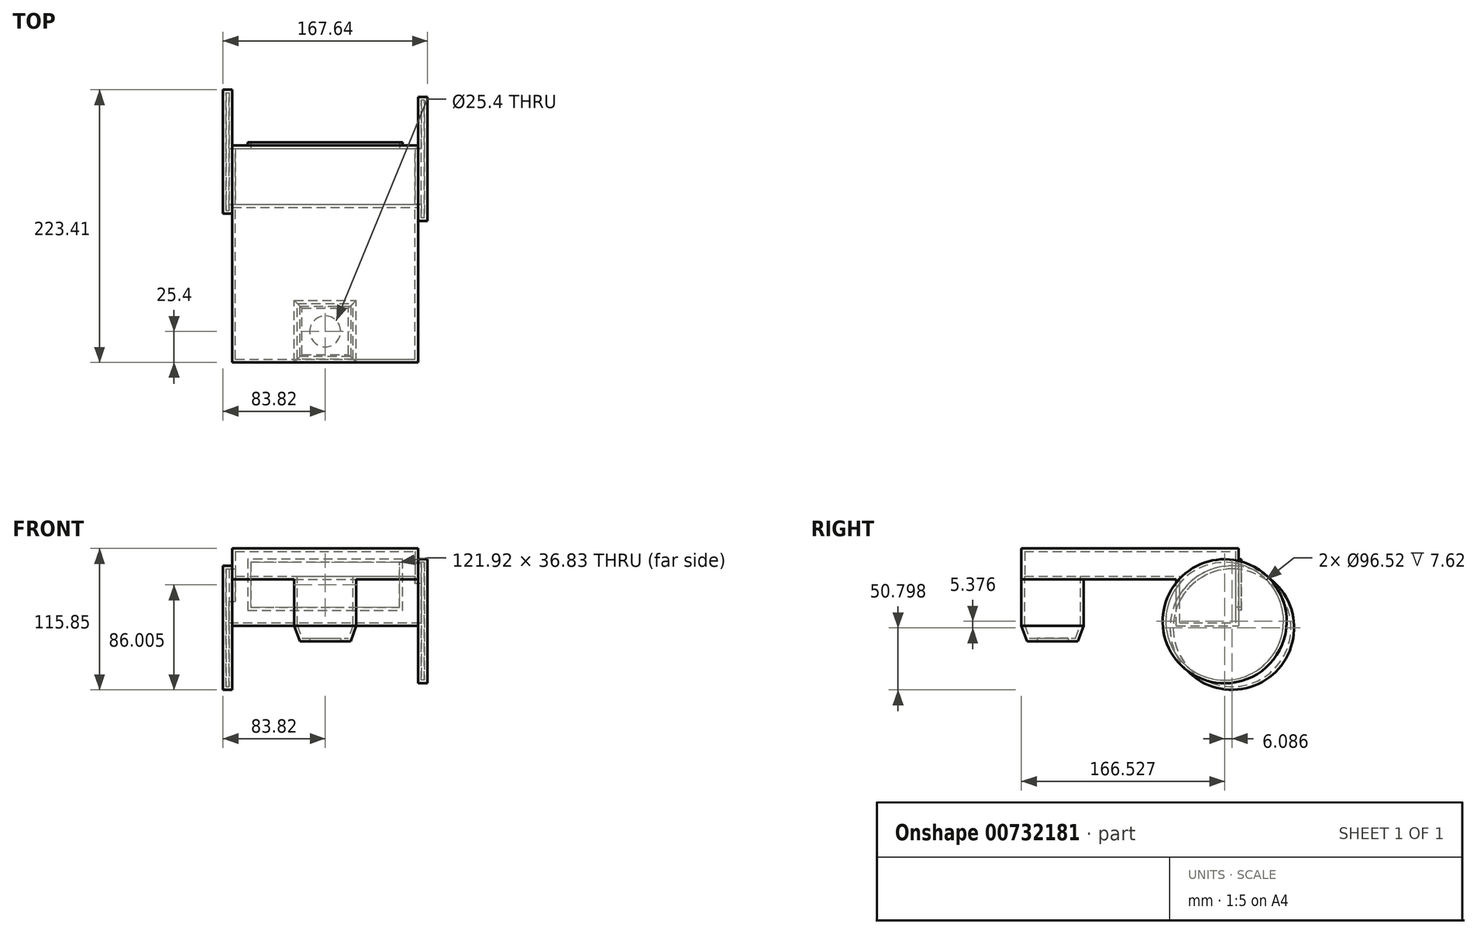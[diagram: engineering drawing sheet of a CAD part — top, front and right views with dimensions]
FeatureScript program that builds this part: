
annotation { "Feature Type Name" : "Feature", "Feature Type Description" : "" }
export const myFeature = defineFeature(function(context is Context, id is Id, definition is map)
    precondition{}
    {
        {
            var Q0;
            Q0=qCreatedBy(makeId("Front.planeOp"),FACE);
            var sketch = newSketch(context, id + "F0", { "sketchPlane" : qUnion([Q0])});
            skLineSegment(sketch, "E0.bottom", {"start": v(-101.6, 25.4) * mm, "end": v(50.8, 25.4) * mm});
            skLineSegment(sketch, "E0.top", {"start": v(-101.6, 0) * mm, "end": v(50.8, 0) * mm});
            skLineSegment(sketch, "E0.left", {"start": v(-101.6, 25.4) * mm, "end": v(-101.6, 0) * mm});
            skLineSegment(sketch, "E0.right", {"start": v(50.8, 25.4) * mm, "end": v(50.8, 0) * mm});
            skSolve(sketch);
        }
        {
            var Q0;
            Q0 = qSketchRegion(id + "F0", true);
            extrude(context, id + "F1", {"entities" : qUnion([Q0]), "depth" : 177.8 * mm, "offsetDistance" : 25.4 * mm});
        }
        {
            var Q0;
            Q0=makeQuery(id+"F1.opExtrude","SWEPT_FACE",FACE,{"disambiguationData":[OSD([sQuery(id+"F0.wireOp",EDGE,"E0.top")])]});
            var sketch = newSketch(context, id + "F2", { "sketchPlane" : qUnion([Q0])});
            skLineSegment(sketch, "E1.bottom", {"start": v(-50.8, 177.8) * mm, "end": v(0, 177.8) * mm});
            skLineSegment(sketch, "E1.top", {"start": v(-50.8, 127) * mm, "end": v(0, 127) * mm});
            skLineSegment(sketch, "E1.left", {"start": v(-50.8, 177.8) * mm, "end": v(-50.8, 127) * mm});
            skLineSegment(sketch, "E1.right", {"start": v(0, 177.8) * mm, "end": v(0, 127) * mm});
            skSolve(sketch);
        }
        {
            var Q0;
            Q0=makeQuery(id+"F2.imprint","IMPRINT",FACE,{"disambiguationData":[TD([[makeQuery(id+"F2.imprint","IMPRINT",EDGE,{"derivedFrom":sQuery(id+"F2.wireOp",EDGE,"E1.bottom")}),-1.0]])]});
            extrude(context, id + "F3", {"entities" : qUnion([Q0]), "operationType" : NewBodyOperationType.ADD, "depth" : 50.8 * mm, "offsetDistance" : 25.4 * mm});
        }
        {
            var Q0;
            Q0=makeQuery(id+"F3.opExtrude","CAP_EDGE",EDGE,{"disambiguationData":[OSD([sQuery(id+"F2.wireOp",EDGE,"E1.bottom")])],"isStart":false});
            var Q1;
            Q1=makeQuery(id+"F3.opExtrude","CAP_EDGE",EDGE,{"disambiguationData":[OSD([sQuery(id+"F2.wireOp",EDGE,"E1.left")])],"isStart":false});
            var Q2;
            Q2=makeQuery(id+"F3.opExtrude","CAP_EDGE",EDGE,{"disambiguationData":[OSD([sQuery(id+"F2.wireOp",EDGE,"E1.right")])],"isStart":false});
            var Q3;
            Q3=makeQuery(id+"F3.opExtrude","CAP_EDGE",EDGE,{"disambiguationData":[OSD([sQuery(id+"F2.wireOp",EDGE,"E1.top")])],"isStart":false});
            chamfer(context, id + "F4", {"entities" : qUnion([Q0, Q1, Q2, Q3]), "chamferType" : ChamferType.OFFSET_ANGLE, "width" : 12.7 * mm, "oppositeDirection" : false, "angle" : 20 * degree, "tangentPropagation" : true});
        }
        {
            var Q0;
            Q0=makeQuery(id+"F1.opExtrude","SWEPT_FACE",FACE,{"disambiguationData":[OSD([sQuery(id+"F0.wireOp",EDGE,"E0.top")])]});
            var sketch = newSketch(context, id + "F5", { "sketchPlane" : qUnion([Q0])});
            skLineSegment(sketch, "E2.bottom", {"start": v(-101.6, 0) * mm, "end": v(-63.5, 0) * mm});
            skLineSegment(sketch, "E2.top", {"start": v(-101.6, 50.8) * mm, "end": v(-63.5, 50.8) * mm});
            skLineSegment(sketch, "E2.left", {"start": v(-101.6, 0) * mm, "end": v(-101.6, 50.8) * mm});
            skLineSegment(sketch, "E2.right", {"start": v(-63.5, 0) * mm, "end": v(-63.5, 50.8) * mm});
            skLineSegment(sketch, "E3.bottom", {"start": v(50.8, 0) * mm, "end": v(12.7, 0) * mm});
            skLineSegment(sketch, "E3.top", {"start": v(50.8, 50.8) * mm, "end": v(12.7, 50.8) * mm});
            skLineSegment(sketch, "E3.left", {"start": v(50.8, 0) * mm, "end": v(50.8, 50.8) * mm});
            skLineSegment(sketch, "E3.right", {"start": v(12.7, 0) * mm, "end": v(12.7, 50.8) * mm});
            skLineSegment(sketch, "E4.bottom", {"start": v(-63.5, 50.8) * mm, "end": v(12.7, 50.8) * mm});
            skLineSegment(sketch, "E4.top", {"start": v(-63.5, 0) * mm, "end": v(12.7, 0) * mm});
            skLineSegment(sketch, "E4.left", {"start": v(-63.5, 50.8) * mm, "end": v(-63.5, 0) * mm});
            skLineSegment(sketch, "E4.right", {"start": v(12.7, 50.8) * mm, "end": v(12.7, 0) * mm});
            skSolve(sketch);
        }
        {
            var Q0;
            Q0=makeQuery(id+"F5.imprint","IMPRINT",FACE,{"disambiguationData":[TD([[makeQuery(id+"F5.imprint","IMPRINT",EDGE,{"derivedFrom":sQuery(id+"F5.wireOp",EDGE,"E3.bottom")}),1.0]])]});
            var Q1;
            Q1=makeQuery(id+"F5.imprint","IMPRINT",FACE,{"disambiguationData":[TD([[makeQuery(id+"F5.imprint","IMPRINT",EDGE,{"derivedFrom":sQuery(id+"F5.wireOp",EDGE,"E2.bottom")}),1.0]])]});
            extrude(context, id + "F6", {"entities" : qUnion([Q0, Q1]), "operationType" : NewBodyOperationType.ADD, "depth" : 38.1 * mm, "offsetDistance" : 25.4 * mm});
        }
        {
            var Q0;
            Q0=makeQuery(id+"F6.boolean.opBoolean","MERGE",FACE,{"derivedFrom":[makeQuery(id+"F1.opExtrude","SWEPT_FACE",FACE,{"disambiguationData":[OSD([sQuery(id+"F0.wireOp",EDGE,"E0.right")])]}),makeQuery(id+"F6.opExtrude","SWEPT_FACE",FACE,{"disambiguationData":[OSD([sQuery(id+"F5.wireOp",EDGE,"E3.left")])]})]});
            var sketch = newSketch(context, id + "F7", { "sketchPlane" : qUnion([Q0])});
            skCircle(sketch, "E5", {"center": v(-11.27, -34.28) * mm, "radius": 50.8 * mm});
            skSolve(sketch);
        }
        {
            var Q0;
            Q0 = qSketchRegion(id + "F7", true);
            extrude(context, id + "F8", {"entities" : qUnion([Q0]), "operationType" : NewBodyOperationType.ADD, "depth" : 7.62 * mm, "offsetDistance" : 25.4 * mm});
        }
        {
            var Q0;
            Q0=makeQuery(id+"F6.boolean.opBoolean","MERGE",FACE,{"derivedFrom":[makeQuery(id+"F1.opExtrude","SWEPT_FACE",FACE,{"disambiguationData":[OSD([sQuery(id+"F0.wireOp",EDGE,"E0.left")])]}),makeQuery(id+"F6.opExtrude","SWEPT_FACE",FACE,{"disambiguationData":[OSD([sQuery(id+"F5.wireOp",EDGE,"E2.left")])]})]});
            var sketch = newSketch(context, id + "F9", { "sketchPlane" : qUnion([Q0])});
            skCircle(sketch, "E6", {"center": v(5.19, -39.65) * mm, "radius": 50.8 * mm});
            skSolve(sketch);
        }
        {
            var Q0;
            Q0 = qSketchRegion(id + "F9", true);
            extrude(context, id + "F10", {"entities" : qUnion([Q0]), "operationType" : NewBodyOperationType.ADD, "depth" : 7.62 * mm, "offsetDistance" : 25.4 * mm});
        }
        {
            var Q0;
            Q0 = qSketchRegion(id + "F5", true);
            extrude(context, id + "F11", {"entities" : qUnion([Q0]), "operationType" : NewBodyOperationType.ADD, "depth" : 38.1 * mm, "offsetDistance" : 25.4 * mm});
        }
        {
            var Q0;
            {var subQ0=sQuery(id+"F5.wireOp",EDGE,"E3.bottom");var subQ1=sQuery(id+"F5.wireOp",EDGE,"E2.bottom");Q0=makeQuery(id+"F11.boolean.opBoolean","MERGE",FACE,{"derivedFrom":[makeQuery(id+"F6.boolean.opBoolean","MERGE",FACE,{"derivedFrom":[makeQuery(id+"F1.opExtrude","CAP_FACE",FACE,{"disambiguationData":[OSD([sQuery(id+"F0.wireOp",EDGE,"E0.bottom"),sQuery(id+"F0.wireOp",EDGE,"E0.top"),sQuery(id+"F0.wireOp",EDGE,"E0.left"),sQuery(id+"F0.wireOp",EDGE,"E0.right")])],"isStart":true}),makeQuery(id+"F6.opExtrude","SWEPT_FACE",FACE,{"disambiguationData":[OSD([subQ1])]}),makeQuery(id+"F6.opExtrude","SWEPT_FACE",FACE,{"disambiguationData":[OSD([subQ0])]})]}),makeQuery(id+"F11.opExtrude","SWEPT_FACE",FACE,{"disambiguationData":[OSD([subQ1,subQ0,sQuery(id+"F5.wireOp",EDGE,"E4.top")])]})]});}
            var sketch = newSketch(context, id + "F12", { "sketchPlane" : qUnion([Q0])});
            skLineSegment(sketch, "E7", {"start": v(-38.1, -33.28) * mm, "end": v(-38.1, 16.51) * mm});
            skLineSegment(sketch, "E8", {"start": v(-38.1, 16.51) * mm, "end": v(88.9, 16.51) * mm});
            skLineSegment(sketch, "E9", {"start": v(88.9, 16.51) * mm, "end": v(88.9, -25.4) * mm});
            skLineSegment(sketch, "E10", {"start": v(88.9, -25.4) * mm, "end": v(-38.1, -25.4) * mm});
            skSolve(sketch);
        }
        {
            var Q0;
            Q0 = qSketchRegion(id + "F12", true);
            extrude(context, id + "F13", {"entities" : qUnion([Q0]), "operationType" : NewBodyOperationType.ADD, "depth" : 2.54 * mm, "offsetDistance" : 25.4 * mm});
        }
        {
            var Q0;
            Q0=makeQuery(id+"F13.opExtrude","CAP_FACE",FACE,{"disambiguationData":[OSD([sQuery(id+"F12.wireOp",EDGE,"E7"),sQuery(id+"F12.wireOp",EDGE,"E8"),sQuery(id+"F12.wireOp",EDGE,"E9"),sQuery(id+"F12.wireOp",EDGE,"E10")])],"isStart":false});
            shell(context, id + "F14", {"entities" : qUnion([Q0]), "thickness" : 2.54 * mm});
        }
        {
            var Q0;
            Q0=makeQuery(id+"F3.opExtrude","CAP_FACE",FACE,{"disambiguationData":[OSD([sQuery(id+"F2.wireOp",EDGE,"E1.bottom"),sQuery(id+"F2.wireOp",EDGE,"E1.top"),sQuery(id+"F2.wireOp",EDGE,"E1.left"),sQuery(id+"F2.wireOp",EDGE,"E1.right")])],"isStart":false});
            var sketch = newSketch(context, id + "F15", { "sketchPlane" : qUnion([Q0])});
            skLineSegment(sketch, "E11.bottom", {"start": v(-46.18, 173.18) * mm, "end": v(-4.62, 173.18) * mm});
            skLineSegment(sketch, "E11.top", {"start": v(-46.18, 131.62) * mm, "end": v(-4.62, 131.62) * mm});
            skLineSegment(sketch, "E11.left", {"start": v(-46.18, 173.18) * mm, "end": v(-46.18, 131.62) * mm});
            skLineSegment(sketch, "E11.right", {"start": v(-4.62, 173.18) * mm, "end": v(-4.62, 131.62) * mm});
            skPoint(sketch, "E12", {"position": v(-25.4, 152.4) * mm});
            skSolve(sketch);
        }
        {
            var Q0;
            Q0=sQuery(id+"F15.wireOp",VERTEX,"E12");
            var Q1;
            Q1=makeQuery(id+"F1.opExtrude","SWEPT_BODY",BODY,{"disambiguationData":[OSD([sQuery(id+"F0.wireOp",EDGE,"E0.bottom"),sQuery(id+"F0.wireOp",EDGE,"E0.top"),sQuery(id+"F0.wireOp",EDGE,"E0.left"),sQuery(id+"F0.wireOp",EDGE,"E0.right")])]});
            hole(context, id + "F16", {"style" : HoleStyle.SIMPLE, "endStyle" : HoleEndStyle.BLIND, "holeDiameter" : 25.4 * mm, "majorDiameter" : 6.35 * mm, "holeDepth" : 25.4 * mm, "isTappedThrough" : true, "tappedDepth" : 12.7 * mm, "tapClearance" : 3, "startFromSketch" : true, "locations" : qUnion([Q0]), "scope" : qUnion([Q1])});
        }
    });
